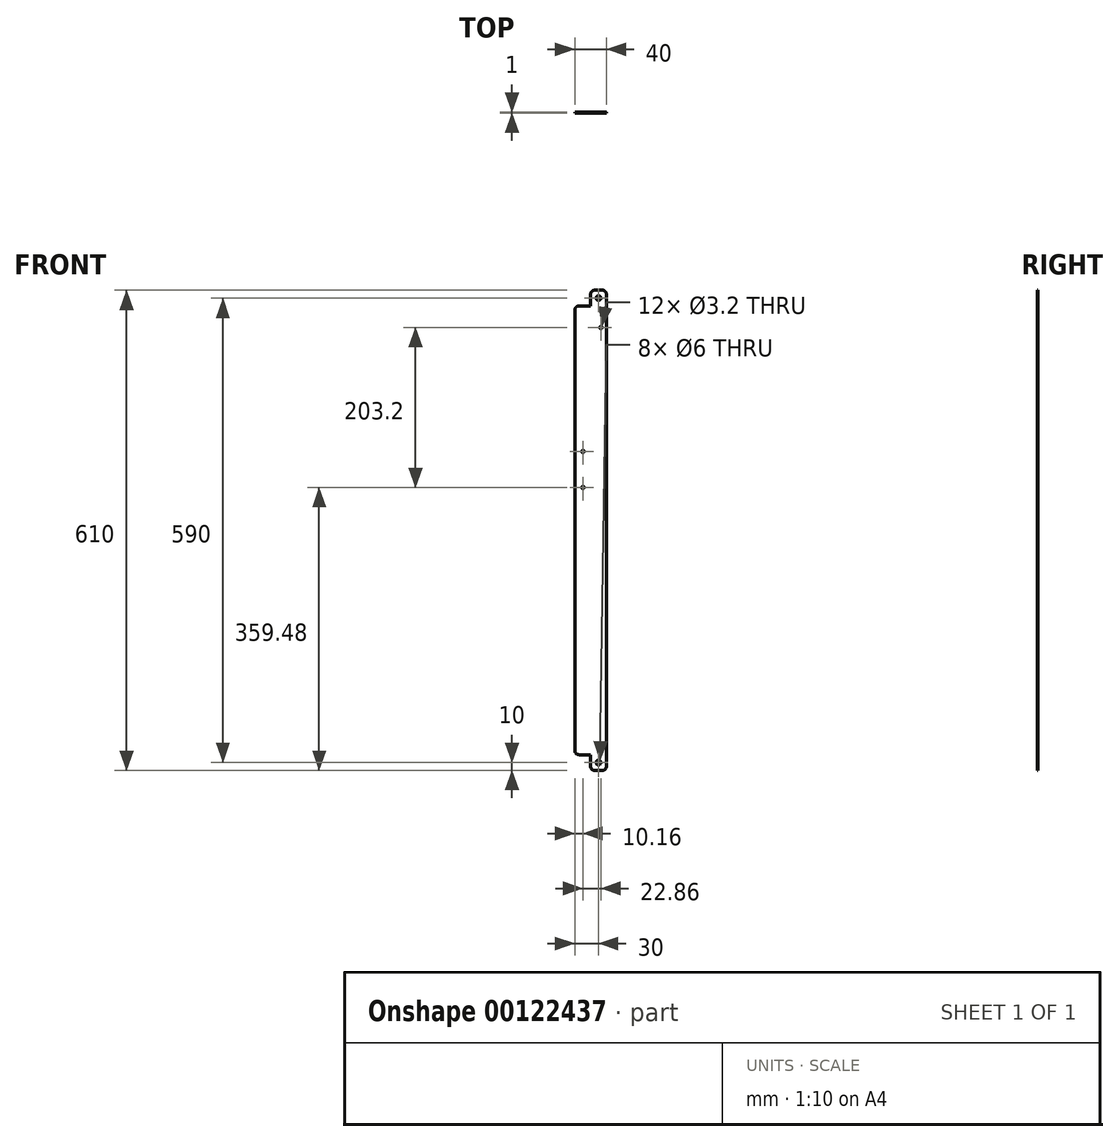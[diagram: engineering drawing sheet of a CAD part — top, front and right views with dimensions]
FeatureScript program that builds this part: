
annotation { "Feature Type Name" : "Feature", "Feature Type Description" : "" }
export const myFeature = defineFeature(function(context is Context, id is Id, definition is map)
    precondition{}
    {
        {
            var Q0;
            Q0=qCreatedBy(makeId("Front.planeOp"),FACE);
            var sketch = newSketch(context, id + "F0", { "sketchPlane" : qUnion([Q0])});
            skLineSegment(sketch, "E0", {"start": v(20, 5) * mm, "end": v(20, 20) * mm});
            skLineSegment(sketch, "E1", {"start": v(20, 20) * mm, "end": v(5, 20) * mm});
            skLineSegment(sketch, "E2", {"start": v(0, 25) * mm, "end": v(0, 585) * mm});
            skLineSegment(sketch, "E3", {"start": v(5, 590) * mm, "end": v(20, 590) * mm});
            skLineSegment(sketch, "E4", {"start": v(20, 590) * mm, "end": v(20, 605) * mm});
            skLineSegment(sketch, "E5", {"start": v(25, 610) * mm, "end": v(35, 610) * mm});
            skLineSegment(sketch, "E6", {"start": v(40, 605) * mm, "end": v(40, 5) * mm});
            skLineSegment(sketch, "E7", {"start": v(35, 0) * mm, "end": v(25, 0) * mm});
            skPoint(sketch, "E8.visualSharp", {"position": v(20, 610) * mm});
            skArc(sketch, "E8.filletArc", {"start": v(25, 610) * mm, "mid": v(21.46, 608.54) * mm, "end": v(20, 605) * mm});
            skPoint(sketch, "E9.visualSharp", {"position": v(40, 610) * mm});
            skArc(sketch, "E9.filletArc", {"start": v(40, 605) * mm, "mid": v(38.54, 608.54) * mm, "end": v(35, 610) * mm});
            skPoint(sketch, "E10.visualSharp", {"position": v(0, 590) * mm});
            skArc(sketch, "E10.filletArc", {"start": v(5, 590) * mm, "mid": v(1.46, 588.54) * mm, "end": v(0, 585) * mm});
            skPoint(sketch, "E11.visualSharp", {"position": v(40, 0) * mm});
            skArc(sketch, "E11.filletArc", {"start": v(35, 0) * mm, "mid": v(38.54, 1.46) * mm, "end": v(40, 5) * mm});
            skPoint(sketch, "E12.visualSharp", {"position": v(20, 0) * mm});
            skArc(sketch, "E12.filletArc", {"start": v(20, 5) * mm, "mid": v(21.46, 1.46) * mm, "end": v(25, 0) * mm});
            skPoint(sketch, "E13.visualSharp", {"position": v(0, 20) * mm});
            skArc(sketch, "E13.filletArc", {"start": v(0, 25) * mm, "mid": v(1.46, 21.46) * mm, "end": v(5, 20) * mm});
            skCircle(sketch, "E14", {"center": v(30, 600) * mm, "radius": 3 * mm});
            skPoint(sketch, "E14.centerSnap0", {"position": v(30, 610) * mm});
            skCircle(sketch, "E15", {"center": v(33.02, 562.68) * mm, "radius": 1.6 * mm});
            skCircle(sketch, "E16", {"center": v(10.16, 405.2) * mm, "radius": 1.6 * mm});
            skCircle(sketch, "E17", {"center": v(10.16, 359.48) * mm, "radius": 1.6 * mm});
            skCircle(sketch, "E18", {"center": v(30, 10) * mm, "radius": 3 * mm});
            skPoint(sketch, "E18.centerSnap0", {"position": v(30, 0) * mm});
            skSolve(sketch);
        }
        {
            var Q0;
            Q0 = qSketchRegion(id + "F0", true);
            extrude(context, id + "F1", {"entities" : qUnion([Q0]), "depth" : 1 * mm});
        }
    });
